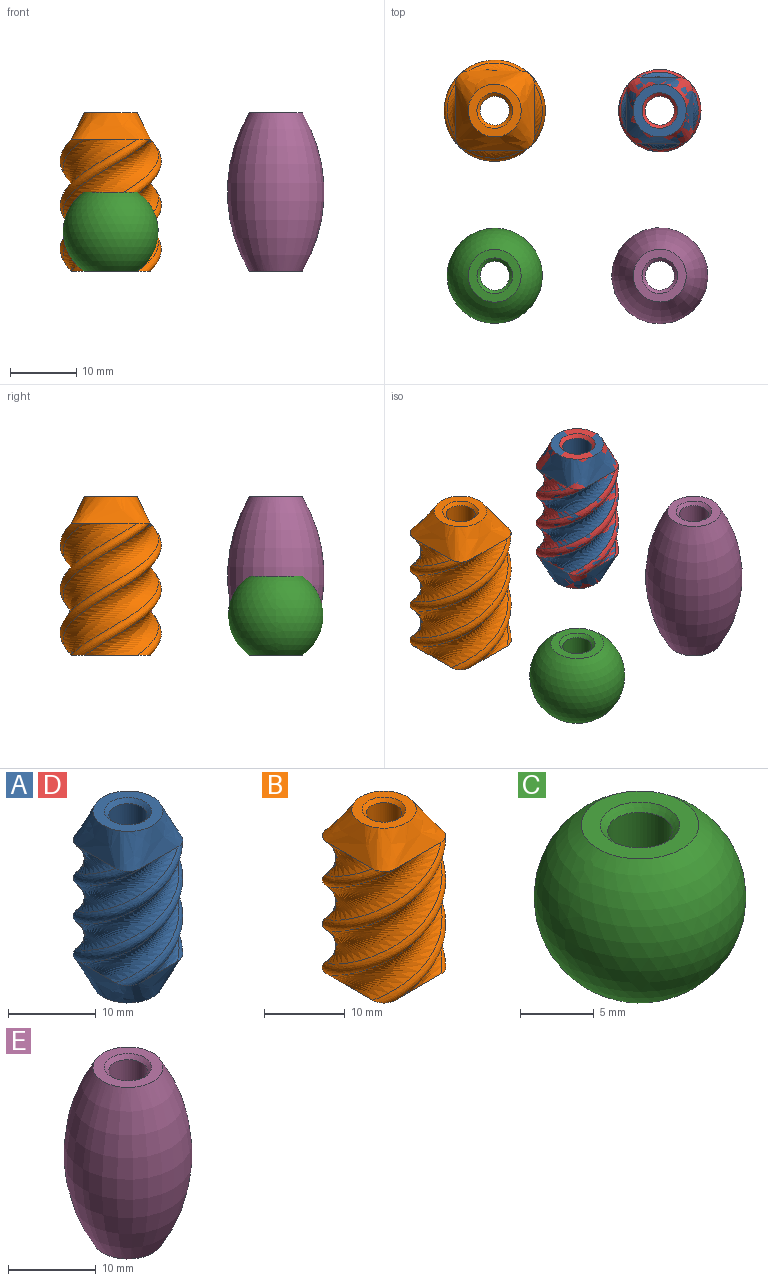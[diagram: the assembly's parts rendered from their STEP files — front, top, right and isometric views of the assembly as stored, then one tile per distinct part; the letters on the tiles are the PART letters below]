
ASSEMBLY  parts=5 mates=3
PART A: 15 faces, bbox 13.8x13.8x24.1 mm
  f0: bspline ~17.07x12.21mm, area 107.4mm2, adj f1,f7,f9,f11
  f1: bspline ~17.07x13.66mm, area 56.7mm2, adj f0,f2,f9,f11
  f2: bspline ~17.07x12.21mm, area 107.4mm2, adj f1,f3,f9,f11
  f3: bspline ~17.07x13.66mm, area 56.7mm2, adj f2,f4,f9,f11
  f4: bspline ~17.07x12.21mm, area 107.4mm2, adj f3,f5,f9,f11
  f5: bspline ~17.07x13.66mm, area 56.7mm2, adj f4,f6,f9,f11
  f6: bspline ~17.07x12.21mm, area 107.4mm2, adj f5,f7,f9,f11
  f7: bspline ~17.07x13.66mm, area 56.7mm2, adj f0,f6,f9,f11
  f8: plane 8.12x8.12mm, normal (0,0,1), area 27.4mm2, adj f9,f14
  f9: bspline ~10x10mm, area 131.8mm2, adj f0,f1,f2,f3,f4,f5,f6,f7
  f10: plane 8.12x8.12mm, normal (0,0,-1), area 27.4mm2, adj f11,f13
  f11: bspline ~10x10mm, area 131.8mm2, adj f0,f1,f2,f3,f4,f5,f6,f7
  f12: cylinder r=2.2mm len=23mm, axis (0,0,1), area 317.9mm2, adj f13,f14
  f13: cone r=2.2mm half-angle=45deg, axis (0,0,-1), area 10.9mm2, adj f10,f12
  f14: cone r=2.2mm half-angle=45deg, axis (0,0,1), area 10.9mm2, adj f8,f12
PART B: 14 faces, bbox 16.7x16.7x24.1 mm
  f0: bspline ~21.33x15.15mm, area 181.3mm2, adj f1,f7,f8,f10
  f1: bspline ~21.33x16.6mm, area 71.9mm2, adj f0,f2,f8,f10
  f2: bspline ~21.33x15.15mm, area 181.3mm2, adj f1,f3,f8,f10
  f3: bspline ~21.33x16.6mm, area 71.9mm2, adj f2,f4,f8,f10
  f4: bspline ~21.33x15.15mm, area 181.3mm2, adj f3,f5,f8,f10
  f5: bspline ~21.33x16.6mm, area 71.9mm2, adj f4,f6,f8,f10
  f6: bspline ~21.33x15.15mm, area 181.3mm2, adj f5,f7,f8,f10
  f7: bspline ~21.33x16.6mm, area 71.9mm2, adj f0,f6,f8,f10
  f8: plane 12.06x12.06mm, normal (0,0,-1), area 117.7mm2, adj f0,f1,f2,f3,f4,f5,f6,f7
  f9: plane 8.15x8.15mm, normal (0,0,1), area 27.4mm2, adj f10,f13
  f10: bspline ~12x12mm, area 166.2mm2, adj f0,f1,f2,f3,f4,f5,f6,f7
  f11: cylinder r=2.2mm len=23mm, axis (0,0,1), area 317.9mm2, adj f12,f13
  f12: cone r=2.7mm half-angle=45deg, axis (0,0,-1), area 10.9mm2, adj f8,f11
  f13: cone r=2.2mm half-angle=45deg, axis (0,0,1), area 10.9mm2, adj f9,f11
PART C: 6 faces, bbox 14.4x14.4x12 mm
  f0: plane 8x8mm, normal (0,0,-1), area 27.4mm2, adj f1,f4
  f1: sphere r=7.21mm, area 543.7mm2, adj f0,f2
  f2: plane 8x8mm, normal (0,0,1), area 27.4mm2, adj f1,f5
  f3: cylinder r=2.2mm len=11mm, axis (0,0,-1), area 152.1mm2, adj f4,f5
  f4: cone r=2.2mm half-angle=45deg, axis (0,0,-1), area 10.9mm2, adj f0,f3
  f5: cone r=2.7mm half-angle=45deg, axis (0,0,1), area 10.9mm2, adj f2,f3
PART D: same geometry as A
PART E: 6 faces, bbox 14.6x14.6x24 mm
  f0: plane 8x8mm, normal (0,0,-1), area 27.4mm2, adj f1,f4
  f1: revolved ~24x14.65mm, area 982.8mm2, adj f0,f2
  f2: plane 8x8mm, normal (0,0,1), area 27.4mm2, adj f1,f5
  f3: cylinder r=2.2mm len=23mm, axis (0,0,-1), area 317.9mm2, adj f4,f5
  f4: cone r=2.2mm half-angle=45deg, axis (0,0,-1), area 10.9mm2, adj f0,f3
  f5: cone r=2.7mm half-angle=45deg, axis (0,0,1), area 10.9mm2, adj f2,f3
PLACE A at identity
PLACE B t=(-25,0,-4)mm
PLACE C t=(-25,-25,-4)mm
PLACE D at identity fixed
PLACE E t=(0,-25,-4)mm
MATE fastened D.f12 <-> B.f8  axis (0,0,-1) through (0,0,-4)mm
MATE fastened C.f3 <-> D.f10  axis (0,0,-1) through (-25,-25,-4)mm
MATE fastened E.f3 <-> D.f10  axis (0,0,-1) through (0,-25,-4)mm
